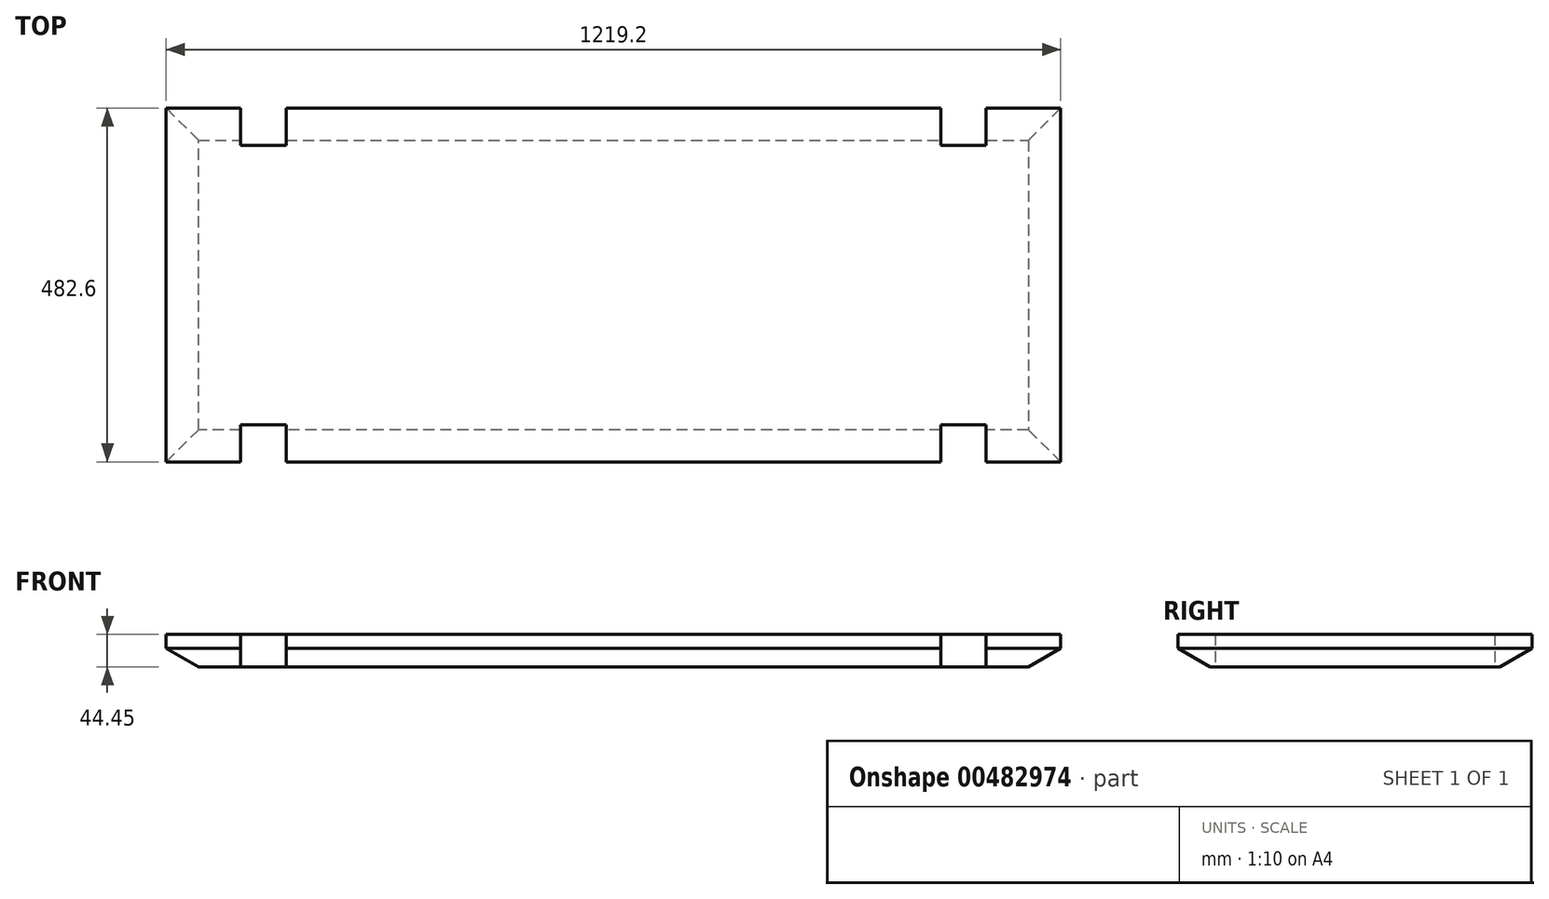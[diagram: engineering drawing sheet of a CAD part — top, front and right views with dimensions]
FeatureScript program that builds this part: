
annotation { "Feature Type Name" : "Feature", "Feature Type Description" : "" }
export const myFeature = defineFeature(function(context is Context, id is Id, definition is map)
    precondition{}
    {
        {
            var Q0;
            Q0=qCreatedBy(makeId("Top.planeOp"),FACE);
            var sketch = newSketch(context, id + "F0", { "sketchPlane" : qUnion([Q0])});
            skLineSegment(sketch, "E0.bottom", {"start": v(-618.2, 257.21) * mm, "end": v(601, 257.21) * mm});
            skLineSegment(sketch, "E0.top", {"start": v(-618.2, -225.39) * mm, "end": v(601, -225.39) * mm});
            skLineSegment(sketch, "E0.left", {"start": v(-618.2, 257.21) * mm, "end": v(-618.2, -225.39) * mm});
            skLineSegment(sketch, "E0.right", {"start": v(601, 257.21) * mm, "end": v(601, -225.39) * mm});
            skLineSegment(sketch, "E1", {"start": v(-516.6, 257.21) * mm, "end": v(-516.6, -225.39) * mm});
            skLineSegment(sketch, "E2", {"start": v(-516.6, -225.39) * mm, "end": v(499.4, -225.39) * mm});
            skLineSegment(sketch, "E3", {"start": v(499.4, -225.39) * mm, "end": v(499.4, 257.21) * mm});
            skLineSegment(sketch, "E4", {"start": v(499.4, 257.21) * mm, "end": v(-516.6, 257.21) * mm});
            skLineSegment(sketch, "E5.bottom", {"start": v(-516.6, 257.21) * mm, "end": v(-454.7, 257.21) * mm});
            skLineSegment(sketch, "E5.top", {"start": v(-516.6, 206.41) * mm, "end": v(-454.7, 206.41) * mm});
            skLineSegment(sketch, "E5.left", {"start": v(-516.6, 257.21) * mm, "end": v(-516.6, 206.41) * mm});
            skLineSegment(sketch, "E5.right", {"start": v(-454.7, 257.21) * mm, "end": v(-454.7, 206.41) * mm});
            skLineSegment(sketch, "E6", {"start": v(-618.2, 15.91) * mm, "end": v(601, 15.91) * mm});
            skLineSegment(sketch, "E7.MirrorCS", {"start": v(-516.6, -225.39) * mm, "end": v(-454.7, -225.39) * mm});
            skLineSegment(sketch, "E8.MirrorCS", {"start": v(-516.6, -225.39) * mm, "end": v(-516.6, -174.59) * mm});
            skLineSegment(sketch, "E9.MirrorCS", {"start": v(-516.6, -174.59) * mm, "end": v(-454.7, -174.59) * mm});
            skLineSegment(sketch, "E10.MirrorCS", {"start": v(-454.7, -225.39) * mm, "end": v(-454.7, -174.59) * mm});
            skLineSegment(sketch, "E11", {"start": v(-8.6, 257.21) * mm, "end": v(0, -225.39) * mm});
            skLineSegment(sketch, "E12.bottom", {"start": v(499.4, 257.21) * mm, "end": v(437.48, 257.21) * mm});
            skLineSegment(sketch, "E12.top", {"start": v(499.4, 206.41) * mm, "end": v(437.48, 206.41) * mm});
            skLineSegment(sketch, "E12.left", {"start": v(499.4, 257.21) * mm, "end": v(499.4, 206.41) * mm});
            skLineSegment(sketch, "E12.right", {"start": v(437.48, 257.21) * mm, "end": v(437.48, 206.41) * mm});
            skLineSegment(sketch, "E13.MirrorCS", {"start": v(499.4, -174.59) * mm, "end": v(437.48, -174.59) * mm});
            skLineSegment(sketch, "E14.MirrorCS", {"start": v(499.4, -225.39) * mm, "end": v(437.48, -225.39) * mm});
            skLineSegment(sketch, "E15.MirrorCS", {"start": v(499.4, -225.39) * mm, "end": v(499.4, -174.59) * mm});
            skLineSegment(sketch, "E16.MirrorCS", {"start": v(437.48, -225.39) * mm, "end": v(437.48, -174.59) * mm});
            skLineSegment(sketch, "E17.bottom", {"start": v(-516.6, -212.69) * mm, "end": v(-454.7, -212.69) * mm});
            skLineSegment(sketch, "E17.top", {"start": v(-516.6, -161.89) * mm, "end": v(-454.7, -161.89) * mm});
            skLineSegment(sketch, "E17.left", {"start": v(-516.6, -212.69) * mm, "end": v(-516.6, -161.89) * mm});
            skLineSegment(sketch, "E17.right", {"start": v(-454.7, -212.69) * mm, "end": v(-454.7, -161.89) * mm});
            skLineSegment(sketch, "E18.bottom", {"start": v(-454.7, 244.51) * mm, "end": v(-516.6, 244.51) * mm});
            skLineSegment(sketch, "E18.top", {"start": v(-454.7, 193.71) * mm, "end": v(-516.6, 193.71) * mm});
            skLineSegment(sketch, "E18.left", {"start": v(-454.7, 244.51) * mm, "end": v(-454.7, 193.71) * mm});
            skLineSegment(sketch, "E18.right", {"start": v(-516.6, 244.51) * mm, "end": v(-516.6, 193.71) * mm});
            skLineSegment(sketch, "E19.bottom", {"start": v(499.4, 244.51) * mm, "end": v(437.48, 244.51) * mm});
            skLineSegment(sketch, "E19.top", {"start": v(499.4, 193.71) * mm, "end": v(437.48, 193.71) * mm});
            skLineSegment(sketch, "E19.left", {"start": v(499.4, 244.51) * mm, "end": v(499.4, 193.71) * mm});
            skLineSegment(sketch, "E19.right", {"start": v(437.48, 244.51) * mm, "end": v(437.48, 193.71) * mm});
            skLineSegment(sketch, "E20.bottom", {"start": v(499.4, -212.69) * mm, "end": v(437.48, -212.69) * mm});
            skLineSegment(sketch, "E20.top", {"start": v(499.4, -161.89) * mm, "end": v(437.48, -161.89) * mm});
            skLineSegment(sketch, "E20.left", {"start": v(499.4, -212.69) * mm, "end": v(499.4, -161.89) * mm});
            skLineSegment(sketch, "E20.right", {"start": v(437.48, -212.69) * mm, "end": v(437.48, -161.89) * mm});
            skSolve(sketch);
        }
        {
            var Q0;
            {var subQ6=sQuery(id+"F0.wireOp",EDGE,"E0.left");var subQ8=sQuery(id+"F0.wireOp",EDGE,"E0.bottom");var subQ9=makeQuery(id+"F0.imprint","INTERSECT",VERTEX,{"derivedFrom":[subQ8,subQ6]});Q0=makeQuery(id+"F0.imprint","IMPRINT",FACE,{"disambiguationData":[TD([[makeQuery(id+"F0.imprint","IMPRINT",EDGE,{"disambiguationData":[TD([[subQ9,-1.0]])],"derivedFrom":subQ8}),-1.0]])]});}
            var Q1;
            {var subQ6=sQuery(id+"F0.wireOp",EDGE,"E0.left");var subQ8=sQuery(id+"F0.wireOp",EDGE,"E0.top");var subQ9=makeQuery(id+"F0.imprint","INTERSECT",VERTEX,{"derivedFrom":[subQ8,subQ6]});Q1=makeQuery(id+"F0.imprint","IMPRINT",FACE,{"disambiguationData":[TD([[makeQuery(id+"F0.imprint","IMPRINT",EDGE,{"disambiguationData":[TD([[subQ9,-1.0]])],"derivedFrom":subQ8}),1.0]])]});}
            var Q2;
            {var subQ3=sQuery(id+"F0.wireOp",EDGE,"E17.top");Q2=makeQuery(id+"F0.imprint","IMPRINT",FACE,{"disambiguationData":[TD([[makeQuery(id+"F0.imprint","IMPRINT",EDGE,{"derivedFrom":subQ3}),1.0]])]});}
            var Q3;
            {var subQ7=sQuery(id+"F0.wireOp",EDGE,"E18.top");Q3=makeQuery(id+"F0.imprint","IMPRINT",FACE,{"disambiguationData":[TD([[makeQuery(id+"F0.imprint","IMPRINT",EDGE,{"derivedFrom":subQ7}),1.0]])]});}
            var Q4;
            {var subQ5=sQuery(id+"F0.wireOp",EDGE,"E20.top");Q4=makeQuery(id+"F0.imprint","IMPRINT",FACE,{"disambiguationData":[TD([[makeQuery(id+"F0.imprint","IMPRINT",EDGE,{"derivedFrom":subQ5}),-1.0]])]});}
            var Q5;
            {var subQ8=sQuery(id+"F0.wireOp",EDGE,"E19.top");Q5=makeQuery(id+"F0.imprint","IMPRINT",FACE,{"disambiguationData":[TD([[makeQuery(id+"F0.imprint","IMPRINT",EDGE,{"derivedFrom":subQ8}),1.0]])]});}
            var Q6;
            {var subQ4=sQuery(id+"F0.wireOp",EDGE,"E0.right");var subQ6=sQuery(id+"F0.wireOp",EDGE,"E0.bottom");var subQ7=makeQuery(id+"F0.imprint","INTERSECT",VERTEX,{"derivedFrom":[subQ6,subQ4]});Q6=makeQuery(id+"F0.imprint","IMPRINT",FACE,{"disambiguationData":[TD([[makeQuery(id+"F0.imprint","IMPRINT",EDGE,{"disambiguationData":[TD([[subQ7,1.0]])],"derivedFrom":subQ6}),-1.0]])]});}
            var Q7;
            {var subQ6=sQuery(id+"F0.wireOp",EDGE,"E0.right");var subQ8=sQuery(id+"F0.wireOp",EDGE,"E0.top");var subQ9=makeQuery(id+"F0.imprint","INTERSECT",VERTEX,{"derivedFrom":[subQ8,subQ6]});Q7=makeQuery(id+"F0.imprint","IMPRINT",FACE,{"disambiguationData":[TD([[makeQuery(id+"F0.imprint","IMPRINT",EDGE,{"disambiguationData":[TD([[subQ9,1.0]])],"derivedFrom":subQ8}),1.0]])]});}
            var Q8;
            {var subQ0=sQuery(id+"F0.wireOp",EDGE,"E13.MirrorCS");Q8=makeQuery(id+"F0.imprint","IMPRINT",FACE,{"disambiguationData":[TD([[makeQuery(id+"F0.imprint","IMPRINT",EDGE,{"derivedFrom":subQ0}),-1.0]])]});}
            var Q9;
            {var subQ0=sQuery(id+"F0.wireOp",EDGE,"E12.top");Q9=makeQuery(id+"F0.imprint","IMPRINT",FACE,{"disambiguationData":[TD([[makeQuery(id+"F0.imprint","IMPRINT",EDGE,{"derivedFrom":subQ0}),1.0]])]});}
            var Q10;
            {var subQ2=sQuery(id+"F0.wireOp",EDGE,"E5.top");Q10=makeQuery(id+"F0.imprint","IMPRINT",FACE,{"disambiguationData":[TD([[makeQuery(id+"F0.imprint","IMPRINT",EDGE,{"derivedFrom":subQ2}),-1.0]])]});}
            var Q11;
            {var subQ0=sQuery(id+"F0.wireOp",EDGE,"E9.MirrorCS");Q11=makeQuery(id+"F0.imprint","IMPRINT",FACE,{"disambiguationData":[TD([[makeQuery(id+"F0.imprint","IMPRINT",EDGE,{"derivedFrom":subQ0}),1.0]])]});}
            extrude(context, id + "F1", {"entities" : qUnion([Q0, Q1, Q2, Q3, Q4, Q5, Q6, Q7, Q8, Q9, Q10, Q11]), "depth" : 44.45 * mm, "offsetDistance" : 25.4 * mm});
        }
        {
            var Q0;
            Q0=makeQuery(id+"F1.opExtrude","CAP_EDGE",EDGE,{"disambiguationData":[OSD([sQuery(id+"F0.wireOp",EDGE,"E0.left")])],"isStart":true});
            var Q1;
            {var subQ0=sQuery(id+"F0.wireOp",EDGE,"E0.top");Q1=makeQuery(id+"F1.opExtrude","CAP_EDGE",EDGE,{"disambiguationData":[OSD([subQ0]),TDD([makeQuery(id+"F0.imprint","IMPRINT",EDGE,{"disambiguationData":[TD([[makeQuery(id+"F0.imprint","INTERSECT",VERTEX,{"derivedFrom":[subQ0,sQuery(id+"F0.wireOp",EDGE,"E0.left")]}),-1.0]])],"derivedFrom":subQ0})])],"isStart":true});}
            var Q2;
            {var subQ0=sQuery(id+"F0.wireOp",EDGE,"E0.top");var subQ1=makeQuery(id+"F0.imprint","INTERSECT",VERTEX,{"derivedFrom":[subQ0,sQuery(id+"F0.wireOp",EDGE,"E11")]});Q2=makeQuery(id+"F1.opExtrude","CAP_EDGE",EDGE,{"disambiguationData":[OSD([subQ0]),TDD([makeQuery(id+"F0.imprint","IMPRINT",EDGE,{"disambiguationData":[TD([[makeQuery(id+"F0.imprint","INTERSECT",VERTEX,{"derivedFrom":[subQ0,sQuery(id+"F0.wireOp",EDGE,"E10.MirrorCS")]}),-1.0]])],"derivedFrom":subQ0}),makeQuery(id+"F0.imprint","IMPRINT",EDGE,{"disambiguationData":[TD([[subQ1,-1.0]])],"derivedFrom":subQ0})])],"isStart":true});}
            var Q3;
            {var subQ0=sQuery(id+"F0.wireOp",EDGE,"E0.top");Q3=makeQuery(id+"F1.opExtrude","CAP_EDGE",EDGE,{"disambiguationData":[OSD([subQ0]),TDD([makeQuery(id+"F0.imprint","IMPRINT",EDGE,{"disambiguationData":[TD([[makeQuery(id+"F0.imprint","INTERSECT",VERTEX,{"derivedFrom":[subQ0,sQuery(id+"F0.wireOp",EDGE,"E0.right")]}),1.0]])],"derivedFrom":subQ0})])],"isStart":true});}
            var Q4;
            Q4=makeQuery(id+"F1.opExtrude","CAP_EDGE",EDGE,{"disambiguationData":[OSD([sQuery(id+"F0.wireOp",EDGE,"E0.right")])],"isStart":true});
            var Q5;
            {var subQ0=sQuery(id+"F0.wireOp",EDGE,"E0.bottom");Q5=makeQuery(id+"F1.opExtrude","CAP_EDGE",EDGE,{"disambiguationData":[OSD([subQ0]),TDD([makeQuery(id+"F0.imprint","IMPRINT",EDGE,{"disambiguationData":[TD([[makeQuery(id+"F0.imprint","INTERSECT",VERTEX,{"derivedFrom":[subQ0,sQuery(id+"F0.wireOp",EDGE,"E0.right")]}),1.0]])],"derivedFrom":subQ0})])],"isStart":true});}
            var Q6;
            {var subQ0=sQuery(id+"F0.wireOp",EDGE,"E0.bottom");var subQ1=makeQuery(id+"F0.imprint","INTERSECT",VERTEX,{"derivedFrom":[subQ0,sQuery(id+"F0.wireOp",EDGE,"E11")]});Q6=makeQuery(id+"F1.opExtrude","CAP_EDGE",EDGE,{"disambiguationData":[OSD([subQ0]),TDD([makeQuery(id+"F0.imprint","IMPRINT",EDGE,{"disambiguationData":[TD([[subQ1,-1.0]])],"derivedFrom":subQ0}),makeQuery(id+"F0.imprint","IMPRINT",EDGE,{"disambiguationData":[TD([[subQ1,1.0]])],"derivedFrom":subQ0})])],"isStart":true});}
            var Q7;
            {var subQ0=sQuery(id+"F0.wireOp",EDGE,"E0.bottom");Q7=makeQuery(id+"F1.opExtrude","CAP_EDGE",EDGE,{"disambiguationData":[OSD([subQ0]),TDD([makeQuery(id+"F0.imprint","IMPRINT",EDGE,{"disambiguationData":[TD([[makeQuery(id+"F0.imprint","INTERSECT",VERTEX,{"derivedFrom":[subQ0,sQuery(id+"F0.wireOp",EDGE,"E0.left")]}),-1.0]])],"derivedFrom":subQ0})])],"isStart":true});}
            chamfer(context, id + "F2", {"entities" : qUnion([Q0, Q1, Q2, Q3, Q4, Q5, Q6, Q7]), "chamferType" : ChamferType.OFFSET_ANGLE, "width" : 25.4 * mm, "oppositeDirection" : false, "angle" : 60 * degree, "tangentPropagation" : true});
        }
    });
